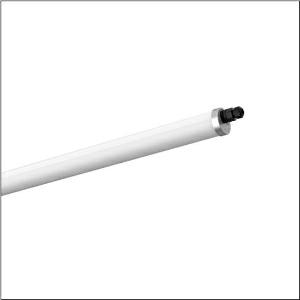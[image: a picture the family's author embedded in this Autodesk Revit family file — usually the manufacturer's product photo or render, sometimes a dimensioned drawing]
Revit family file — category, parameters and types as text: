
# Revit family: monsun_r__31_tube_51ft107n4a0a_c9dd
name_source: partatom
category: Lighting Fixtures
units: mm (PartAtom-declared; Revit-internal decimal feet)

## family parameters
Cut with Voids When Loaded = No
Host = Face
Light Source = No
Part Type = Normal
Room Calculation Point = No
Round Connector Dimension = Use Diameter
Shared = No

## types (1)
- Monsun® 31 Tube (1 x LED, 10000 lm, 58 W, 4000K)
    Apparent Load = 58 VA
    CIE Flux Codes = 42 71 90 91 100
    Color Rendering = 80
    Color Temperature = 4000K
    Default Elevation = 1800 mm
    Description = Monsun® 31 Tube, tubular luminaire, primary optical cover: diffuser, of PMMA, light emission: direct distribution, primary light characteristic: symmetric, installation type: suspended mounting, surface-mounted, LED, rated luminous flux: 10.000lm, luminous efficacy: 160lm/W, light colour: 840, colour temperature: 4000K, with with 1 terminal, 3-pole, max. 2.5mm², through-wiring: 3x 1.5mm², mains connection: 220..240V, AC, 50/60Hz, rated input power: 58W, housing, cylindrical, of PMMA, semi-transparent, matt white, with luminaire and ceiling fastening, V4A, mounting with brackets of stainless steel, length: 1.560mm, diameter: 75mm, end cap, of stainless steel (V4A), protection rating (complete): IP67/IP69K, insulation class (complete): insulation class I (protective earthing), certification: CE, UKCA, impact resistance: IK07, permissible operating ambient temperature: -20..+40°C, corresponds to IFS (International Featured Standards) requirements for safety and quality in the food industry, usage in unprotected outdoor area possible with horizontal mounting, contact your sales advisor before using the luminaires in applications with unclear chemical exposure, large temperature fluctuations or condensation-forming humidity, packaging unit: 1 piece
    Height = 83 mm
    Lamp = 1 x LED
    Lamp Light Flux = 10000 lm
    Lamp Power = 58 W
    Lamp count = 1
    Length = 1560 mm
    Luminous efficacy = 172 lm/W
    Manufacturer = Siteco
    ModVariant = No
    Model = 51FT107N4A0A
    Mounting Place = Ceiling
    Mounting Type = Pendant
    Number of Poles = 1
    OnlyDefault = Yes
    Power Factor = 1
    Product Name = Monsun® 31 Tube
    Product group = tubular luminaire
    ProductGroupID = 906
    Protection Class = Protection class I
    RLX_Detail_Level = 1
    RLX_Emergency_Light_Flux = 0 lm
    RLX_Emergency_Type = 0
    RLX_Emergency_Type_DB = No
    RlxData = <blob elided: 25357 chars, md5=9b10ba41>
    Socket = socket
    Standby Power = 0 W
    System Light Flux = 10000 lm
    System Power = 58 W
    Type Comments = Product without accessories
    Type Image = l_1228461.jpg
    URL = http://relux.com
    VarID = ---
    Voltage = 0 V
    Weight = 0.00 kg
    Width = 75 mm

## geometry (parser evidence)
native form markers: Blend x4, Sweep x16
no freeform markers — native parametric forms only
